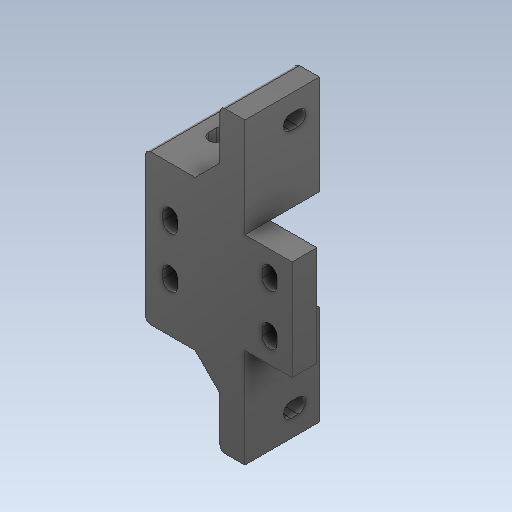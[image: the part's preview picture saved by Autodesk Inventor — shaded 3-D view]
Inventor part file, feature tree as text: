
AUTODESK INVENTOR PART (.ipt)
format: ipt  version: 2020 (Build 240168000, 168)  size: 258,048 bytes
history: native  units: mm
features: extrude x6, sketch x6, mirror x2, chamfer x1, plane x1, fillet x1, projected_geometry x1
ambient origin geometry x8: Origin, YZ Plane, XZ Plane, XY Plane, X Axis, Y Axis, Z Axis, Center Point
bodies: Solid1 (feature_tree)
feature tree (18):
  extrude  "Extrusion1"  Depth=40.0mm
  extrude  "Extrusion2"  Depth=20.0mm TaperAngle=0.0deg
  extrude  "Extrusion3"  Depth=3.0mm
  chamfer  "Chamfer1"  [1 undecoded]
  extrude  "Extrusion7"  Depth=6.0mm
  plane  "Work Plane2"
  mirror  "Mirror2"
  extrude  "Extrusion8"  Depth=10.0mm
  mirror  "Mirror3"
  extrude  "Extrusion9"  Depth=10.0mm
  fillet  "Fillet2"  [1 undecoded]
  sketch  "Sketch1"  dims[d0=10.0mm d1=40.0mm]
  sketch  "Sketch2"  dims[d2=40.0mm d3=20.0mm d4=0.0mm]
  sketch  "Sketch3"  dims[d5=6.0mm d6=3.0mm]
  sketch  "Sketch10"  dims[d7=10.0mm]
  sketch  "Sketch11"  dims[d8=10.0mm d9=0.0mm d10=0.0mm]
  projected_geometry  "Projected Loop2"
  sketch  "Sketch12"  dims[d11=3.0mm d12=6.0mm d13=10.0mm d14=10.0mm d15=0.0mm d16=0.0mm d17=10.0mm d18=2.0mm d19=45.0deg d30=80.3mm d31=120.3mm d32=10.0mm d33=0.0mm d34=-60.15mm d35=20.0mm d36=0.0mm d37=40.3mm d38=19.0mm d39=3.0mm d40=10.0mm d41=10.0mm d42=6.0mm d43=9.0mm d44=0.0mm d45=0.0mm d46=2.0mm]
note: 2 required parameter values undecoded (feature->parameter linkage not recoverable at this tier; creation-order binding heuristic only, values carry confidence <= 0.55)
